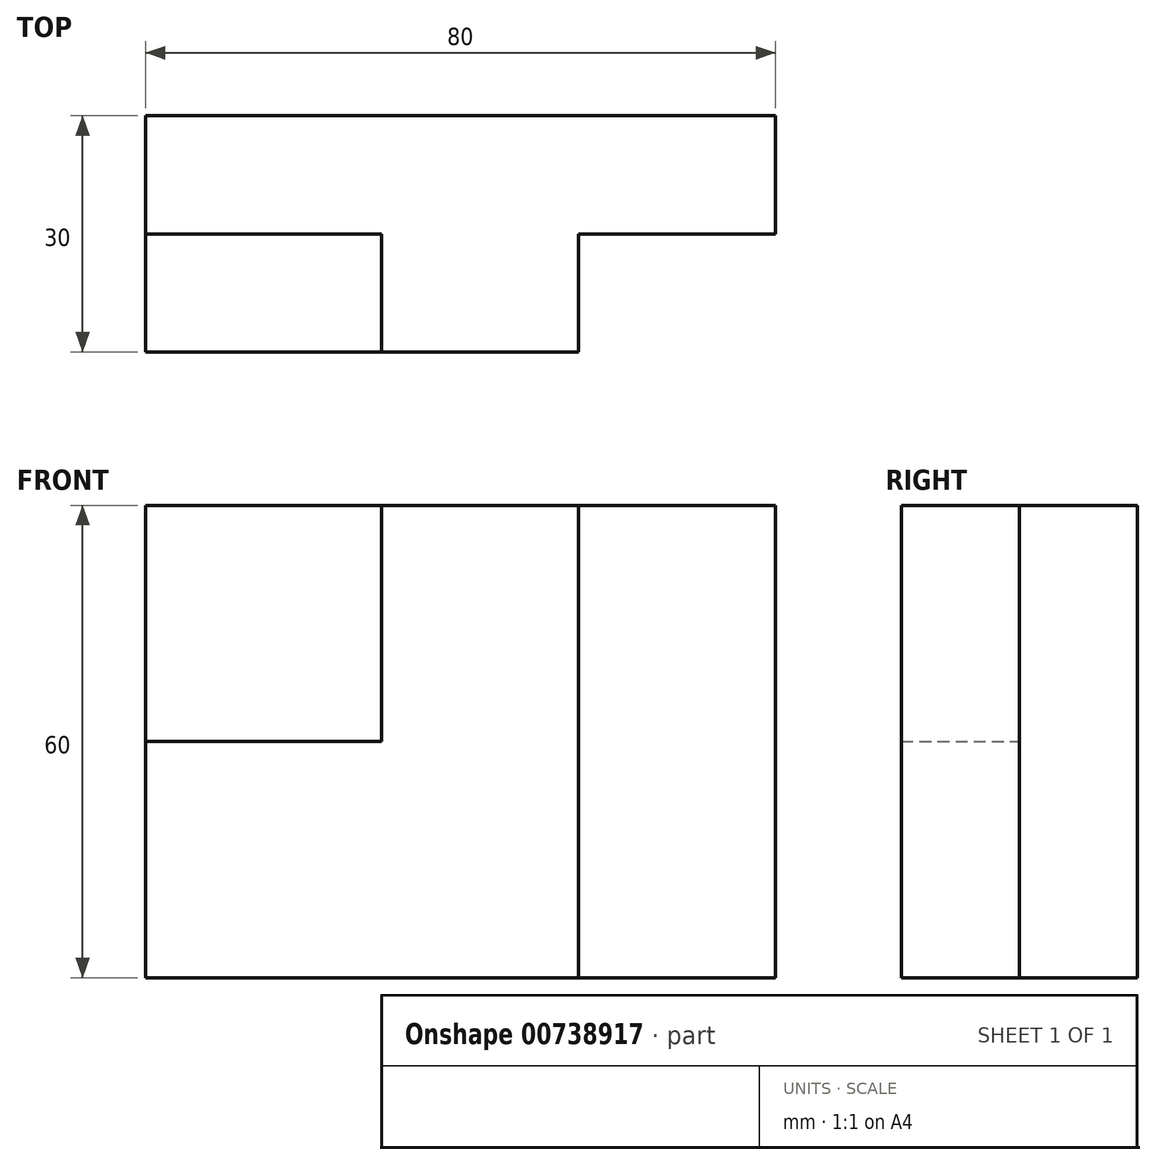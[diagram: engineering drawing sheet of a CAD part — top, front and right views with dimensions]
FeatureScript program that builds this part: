
annotation { "Feature Type Name" : "Feature", "Feature Type Description" : "" }
export const myFeature = defineFeature(function(context is Context, id is Id, definition is map)
    precondition{}
    {
        {
            var Q0;
            Q0=qCreatedBy(makeId("Front.planeOp"),FACE);
            var sketch = newSketch(context, id + "F0", { "sketchPlane" : qUnion([Q0])});
            skLineSegment(sketch, "E0.bottom", {"start": v(0, 0) * mm, "end": v(-80, 0) * mm});
            skLineSegment(sketch, "E0.top", {"start": v(0, 60) * mm, "end": v(-80, 60) * mm});
            skLineSegment(sketch, "E0.left", {"start": v(0, 0) * mm, "end": v(0, 60) * mm});
            skLineSegment(sketch, "E0.right", {"start": v(-80, 0) * mm, "end": v(-80, 60) * mm});
            skSolve(sketch);
        }
        {
            var Q0;
            Q0 = qSketchRegion(id + "F0", true);
            extrude(context, id + "F1", {"entities" : qUnion([Q0]), "depth" : 15 * mm, "offsetDistance" : 25 * mm});
        }
        {
            var Q0;
            Q0=makeQuery(id+"F1.opExtrude","CAP_FACE",FACE,{"disambiguationData":[OSD([sQuery(id+"F0.wireOp",EDGE,"E0.bottom"),sQuery(id+"F0.wireOp",EDGE,"E0.top"),sQuery(id+"F0.wireOp",EDGE,"E0.left"),sQuery(id+"F0.wireOp",EDGE,"E0.right")])],"isStart":false});
            var sketch = newSketch(context, id + "F2", { "sketchPlane" : qUnion([Q0])});
            skLineSegment(sketch, "E1", {"start": v(-25, 0) * mm, "end": v(-25, 60) * mm});
            skLineSegment(sketch, "E2", {"start": v(-50, 60) * mm, "end": v(-50, 30) * mm});
            skLineSegment(sketch, "E3", {"start": v(-50, 30) * mm, "end": v(-80, 30) * mm});
            skLineSegment(sketch, "E4", {"start": v(-80, 30) * mm, "end": v(-80, 0) * mm});
            skLineSegment(sketch, "E5", {"start": v(-80, 0) * mm, "end": v(-25, 0) * mm});
            skLineSegment(sketch, "E6", {"start": v(-50, 60) * mm, "end": v(-25, 60) * mm});
            skSolve(sketch);
        }
        {
            var Q0;
            Q0 = qSketchRegion(id + "F2", true);
            extrude(context, id + "F3", {"entities" : qUnion([Q0]), "operationType" : NewBodyOperationType.ADD, "depth" : 15 * mm, "offsetDistance" : 25 * mm});
        }
    });
